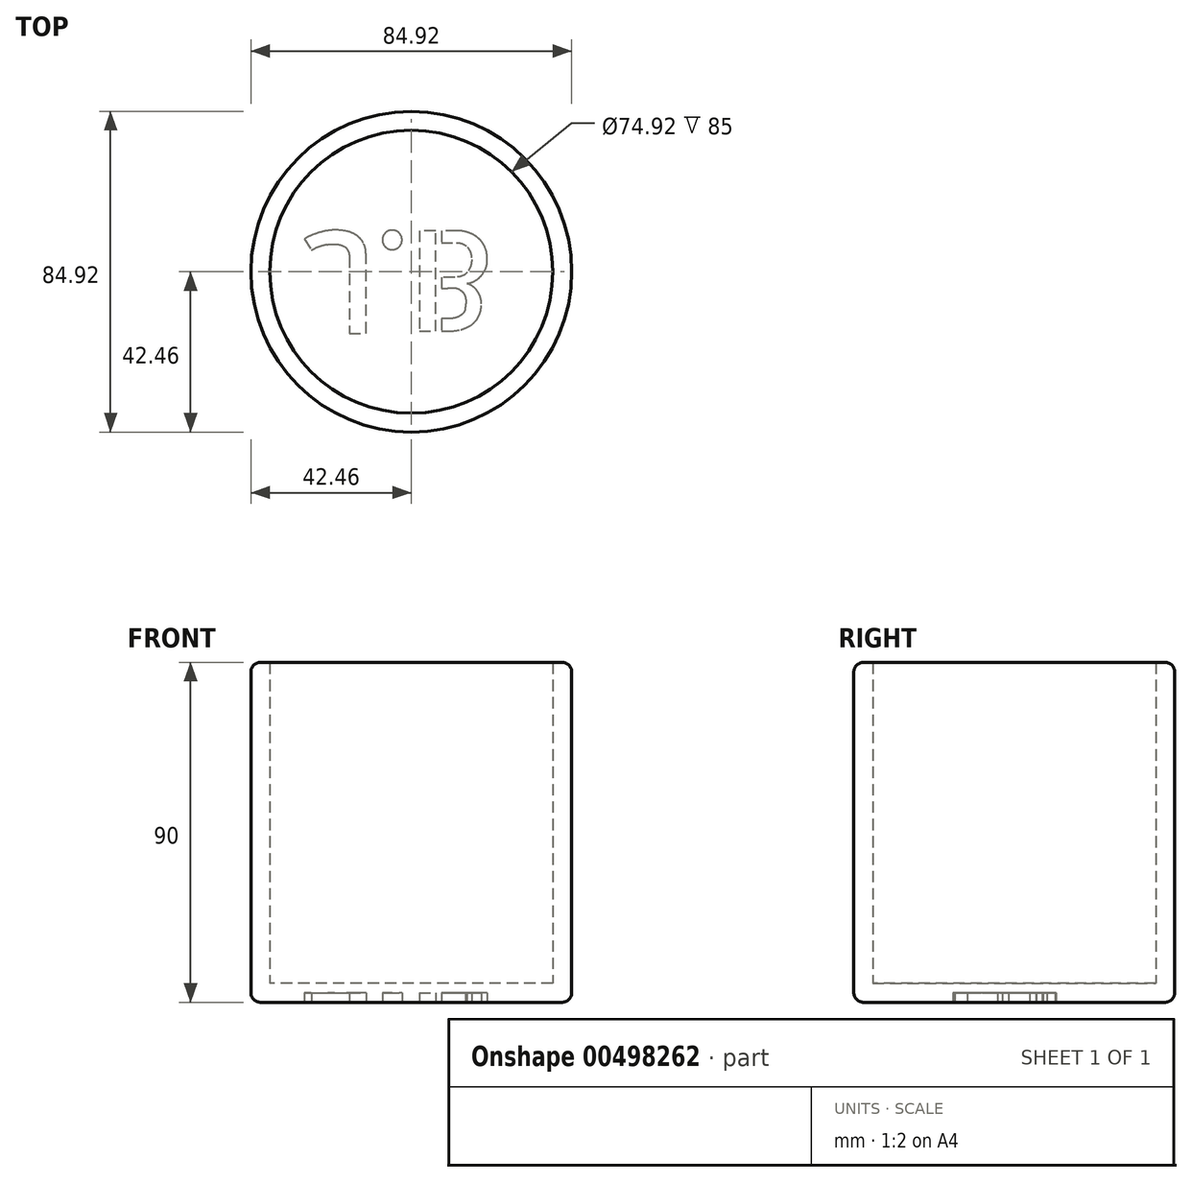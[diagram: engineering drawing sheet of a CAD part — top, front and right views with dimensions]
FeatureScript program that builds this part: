
annotation { "Feature Type Name" : "Feature", "Feature Type Description" : "" }
export const myFeature = defineFeature(function(context is Context, id is Id, definition is map)
    precondition{}
    {
        {
            var Q0;
            Q0=qCreatedBy(makeId("Top.planeOp"),FACE);
            var sketch = newSketch(context, id + "F0", { "sketchPlane" : qUnion([Q0])});
            skCircle(sketch, "E0", {"center": v(0, 0) * mm, "radius": 42.46 * mm});
            skSolve(sketch);
        }
        {
            var Q0;
            Q0=makeQuery(id+"F0.imprint","IMPRINT",FACE,{"disambiguationData":[TD([[makeQuery(id+"F0.imprint","IMPRINT",EDGE,{"derivedFrom":sQuery(id+"F0.wireOp",EDGE,"E0")}),1.0]])]});
            extrude(context, id + "F1", {"entities" : qUnion([Q0]), "depth" : 90 * mm});
        }
        {
            var Q0;
            Q0=makeQuery(id+"F1.opExtrude","CAP_FACE",FACE,{"disambiguationData":[OSD([sQuery(id+"F0.wireOp",EDGE,"E0")])],"isStart":false});
            shell(context, id + "F2", {"entities" : qUnion([Q0]), "thickness" : 5 * mm});
        }
        {
            var Q0;
            Q0=qCreatedBy(makeId("Right.planeOp"),FACE);
            cPlane(context, id + "F3", {"entities" : qUnion([Q0]), "cplaneType" : CPlaneType.OFFSET, "offset" : 37.5 * mm, "width" : 150 * mm, "height" : 150 * mm});
        }
        {
            var Q0;
            Q0=qCreatedBy(id+"F3.planeOp",FACE);
            var sketch = newSketch(context, id + "F4", { "sketchPlane" : qUnion([Q0])});
            skCircle(sketch, "E1", {"center": v(0, 140.14) * mm, "radius": 10.24 * mm});
            skLineSegment(sketch, "E2", {"start": v(0, 70) * mm, "end": v(119.45, 70) * mm});
            skLineSegment(sketch, "E3", {"start": v(0, 40) * mm, "end": v(38.72, 40) * mm});
            skCircle(sketch, "E4", {"center": v(0, 70) * mm, "radius": 5.14 * mm});
            skSolve(sketch);
        }
        {
            var Q0;
            Q0=sQuery(id+"F4.wireOp",EDGE,"E4");
            var Q1;
            Q1=sQuery(id+"F4.wireOp",EDGE,"E3");
            revolve(context, id + "F5", {"bodyType" : ToolBodyType.SURFACE, "surfaceEntities" : qUnion([Q0]), "axis" : qUnion([Q1]), "revolveType" : RevolveType.ONE_DIRECTION, "angle" : 180 * degree});
        }
        {
            var Q0;
            Q0=makeQuery(id+"F1.opExtrude","CAP_EDGE",EDGE,{"disambiguationData":[OSD([sQuery(id+"F0.wireOp",EDGE,"E0")])],"isStart":false});
            var Q1;
            Q1=makeQuery(id+"F1.opExtrude","CAP_EDGE",EDGE,{"disambiguationData":[OSD([sQuery(id+"F0.wireOp",EDGE,"E0")])],"isStart":true});
            fillet(context, id + "F6", {"entities" : qUnion([Q0, Q1]), "radius" : 2.5 * mm, "tangentPropagation" : true, "allowEdgeOverflow" : false});
        }
        {
            var Q0;
            Q0=makeQuery(id+"F1.opExtrude","CAP_FACE",FACE,{"disambiguationData":[OSD([sQuery(id+"F0.wireOp",EDGE,"E0")])],"isStart":true});
            var sketch = newSketch(context, id + "F7", { "sketchPlane" : qUnion([Q0])});
            skText(sketch, "E5", { "text": "J.B\n", "fontName": "AllertaStencil-Regular.ttf"});
            const initialGuessF7  = {"E5": [-0.02923, -0.01088, 1, 0, 0.02663]};
            skSetInitialGuess(sketch, initialGuessF7);
            skSolve(sketch);
        }
        {
            var Q0;
            Q0 = qSketchRegion(id + "F7", true);
            extrude(context, id + "F8", {"entities" : qUnion([Q0]), "operationType" : NewBodyOperationType.REMOVE, "oppositeDirection" : true, "depth" : 2.5 * mm});
        }
    });
